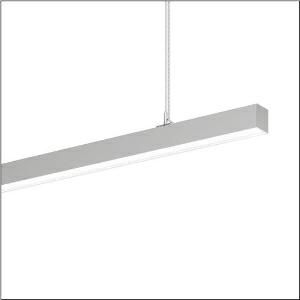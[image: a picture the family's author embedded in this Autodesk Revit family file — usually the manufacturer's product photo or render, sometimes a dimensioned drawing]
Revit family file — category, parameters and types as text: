
# Revit family: silica_r__21_51mx30db35sb_46d1
name_source: partatom
category: Lighting Fixtures
units: mm (PartAtom-declared; Revit-internal decimal feet)

## family parameters
Cut with Voids When Loaded = No
Host = Face
Light Source = No
Part Type = Normal
Room Calculation Point = No
Round Connector Dimension = Use Diameter
Shared = No

## types (1)
- --- (1 x LED, 5260 lm, 34.1 W, 3000K)
    Apparent Load = 34 VA
    CIE Flux Codes = 47 79 96 57 100
    Color Rendering = 80
    Color Temperature = 3000K
    Default Elevation = 1800 mm
    Description = Silica® 21, office luminaire, primary optical cover: cover, of PMMA, opal, light emission: direct/indirect distribution, primary light characteristic: symmetric, installation type: suspended mounting, LED, rated luminous flux: 5.260lm, luminous efficacy: 154lm/W, light colour: 830, colour temperature: 3000K, with terminal, 3+2-pole, max. 2.5mm², mains connection: 220..240V, AC, 50/60Hz, rated input power: 34.1W, luminaire housing, of aluminium, metallic grey (RAL 9006), length: 1.504mm, width: 53mm, height: 53mm, protection rating (complete): IP20, insulation class (complete): insulation class I (protective earthing), certification: CE, permissible operating ambient temperature: 0..+35°C, standard: EN 50419, packaging unit: 1 piece
    Height = 53 mm
    Lamp = 1 x LED
    Lamp Light Flux = 5260 lm
    Lamp Power = 34.1 W
    Lamp count = 1
    Length = 1504 mm
    Luminous efficacy = 154 lm/W
    Manufacturer = Siteco
    ModVariant = No
    Model = 51MX30DB35SB
    Mounting Place = Ceiling
    Mounting Type = Pendant
    Number of Poles = 1
    OnlyDefault = Yes
    Power Factor = 1
    Product Name = Silica® 21
    Product group = office luminaire | ceiling pendant
    ProductGroupID = 902
    Protection Class = Protection class I
    Protection Degree = IP 20
    RLX_Detail_Level = 1
    RLX_Emergency_Light_Flux = 0 lm
    RLX_Emergency_Type = 0
    RLX_Emergency_Type_DB = No
    RlxData = <blob elided: 23433 chars, md5=788a5ac2>
    Socket = socket
    Standby Power = 0 W
    System Light Flux = 5260 lm
    System Power = 34 W
    Type Comments = factory setting: luminous flux: 100 % | dim-lin: 254 | 233 mA
    Type Image = l_1297747.jpg
    URL = http://relux.com
    VarID = @adj_046933
    Voltage = 0 V
    Weight = 0.00 kg
    Width = 53 mm

## geometry (parser evidence)
native form markers: Blend x4, Sweep x13
no freeform markers — native parametric forms only
